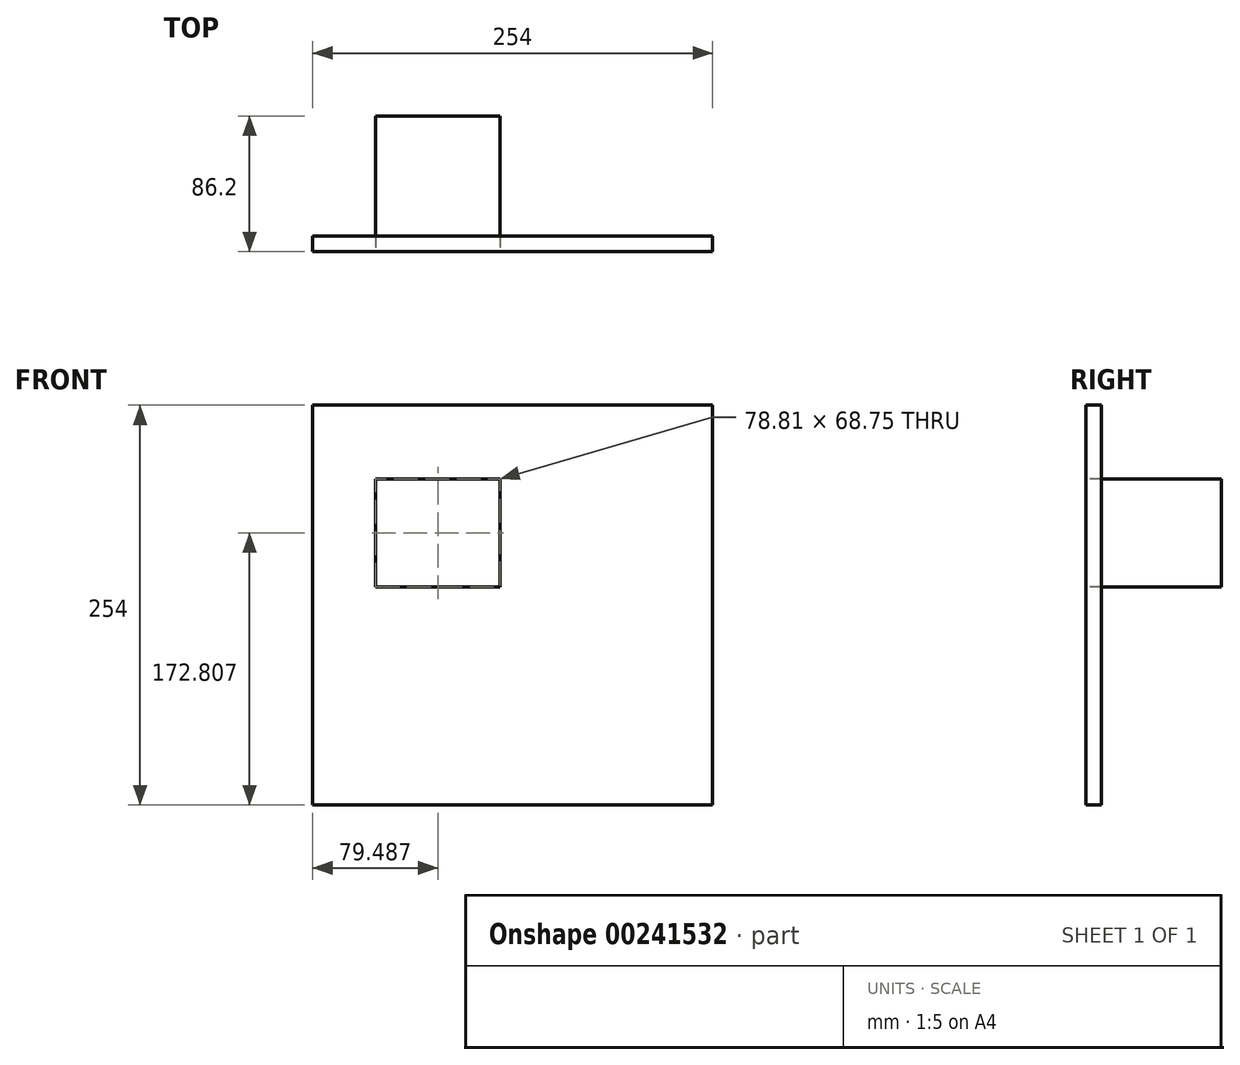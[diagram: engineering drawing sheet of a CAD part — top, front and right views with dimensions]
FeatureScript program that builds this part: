
annotation { "Feature Type Name" : "Feature", "Feature Type Description" : "" }
export const myFeature = defineFeature(function(context is Context, id is Id, definition is map)
    precondition{}
    {
        {
            assignVariable(context, id + "F0", {"name" : "L1", "anyValue" : 10});
        }
        {
            var Q0;
            Q0=qCreatedBy(makeId("Front.planeOp"),FACE);
            var sketch = newSketch(context, id + "F1", { "sketchPlane" : qUnion([Q0])});
            skLineSegment(sketch, "E0.bottom", {"start": v(-23.93, 230.8) * mm, "end": v(230.07, 230.8) * mm});
            skLineSegment(sketch, "E0.top", {"start": v(-23.93, -23.2) * mm, "end": v(230.07, -23.2) * mm});
            skLineSegment(sketch, "E0.left", {"start": v(-23.93, 230.8) * mm, "end": v(-23.93, -23.2) * mm});
            skLineSegment(sketch, "E0.right", {"start": v(230.07, 230.8) * mm, "end": v(230.07, -23.2) * mm});
            skSolve(sketch);
        }
        {
            var Q0;
            Q0 = qSketchRegion(id + "F1", true);
            extrude(context, id + "F2", {"entities" : qUnion([Q0]), "endBound" : BoundingType.SYMMETRIC, "depth" : (getVariable(context, 'L1')) * mm});
        }
        {
            var Q0;
            Q0=makeQuery(id+"F2.opExtrude","CAP_FACE",FACE,{"disambiguationData":[OSD([sQuery(id+"F1.wireOp",EDGE,"E0.bottom"),sQuery(id+"F1.wireOp",EDGE,"E0.top"),sQuery(id+"F1.wireOp",EDGE,"E0.left"),sQuery(id+"F1.wireOp",EDGE,"E0.right")])],"isStart":false});
            var sketch = newSketch(context, id + "F3", { "sketchPlane" : qUnion([Q0])});
            skLineSegment(sketch, "E1.bottom", {"start": v(16.15, 183.98) * mm, "end": v(94.96, 183.98) * mm});
            skLineSegment(sketch, "E1.top", {"start": v(16.15, 115.23) * mm, "end": v(94.96, 115.23) * mm});
            skLineSegment(sketch, "E1.left", {"start": v(16.15, 183.98) * mm, "end": v(16.15, 115.23) * mm});
            skLineSegment(sketch, "E1.right", {"start": v(94.96, 183.98) * mm, "end": v(94.96, 115.23) * mm});
            skSolve(sketch);
        }
        {
            var Q0;
            Q0 = qSketchRegion(id + "F3", true);
            extrude(context, id + "F4", {"entities" : qUnion([Q0]), "operationType" : NewBodyOperationType.REMOVE, "oppositeDirection" : true, "depth" : 76.2 * mm});
        }
        {
            var Q0;
            Q0=makeQuery(id+"F2.opExtrude","CAP_FACE",FACE,{"disambiguationData":[OSD([sQuery(id+"F1.wireOp",EDGE,"E0.bottom"),sQuery(id+"F1.wireOp",EDGE,"E0.top"),sQuery(id+"F1.wireOp",EDGE,"E0.left"),sQuery(id+"F1.wireOp",EDGE,"E0.right")])],"isStart":true});
            var sketch = newSketch(context, id + "F5", { "sketchPlane" : qUnion([Q0])});
            skLineSegment(sketch, "E2.0", {"start": v(-16.15, 183.98) * mm, "end": v(-94.96, 183.98) * mm});
            skLineSegment(sketch, "E3.0", {"start": v(-94.96, 183.98) * mm, "end": v(-94.96, 115.23) * mm});
            skLineSegment(sketch, "E4.0", {"start": v(-16.15, 115.23) * mm, "end": v(-94.96, 115.23) * mm});
            skLineSegment(sketch, "E5.0", {"start": v(-16.15, 183.98) * mm, "end": v(-16.15, 115.23) * mm});
            skSolve(sketch);
        }
        {
            var Q0;
            Q0=makeQuery(id+"F5.imprint","IMPRINT",FACE,{"disambiguationData":[TD([[makeQuery(id+"F5.imprint","IMPRINT",EDGE,{"derivedFrom":sQuery(id+"F5.wireOp",EDGE,"E2.0")}),1.0]])]});
            extrude(context, id + "F6", {"entities" : qUnion([Q0]), "depth" : 76.2 * mm});
        }
    });
